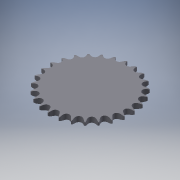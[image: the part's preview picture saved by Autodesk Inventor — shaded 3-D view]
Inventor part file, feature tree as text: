
AUTODESK INVENTOR PART (.ipt)
format: ipt  version: 2016 (Build 200138000, 138)  size: 720,384 bytes
history: native  units: mm
features: other x6, extrude x2, pattern_linear x1, pattern_circular x1
ambient origin geometry x8: Origin, YZ Plane, XZ Plane, XY Plane, X Axis, Y Axis, Z Axis, Center Point
bodies: Solid1 (feature_tree)
feature tree (10):
  other  "Theoretical Tooth Profile"
  other  "Tooth Profile"
  other  "Section Profile"
  other  "Shroud"
  other  "Strand"
  pattern_linear  "Strand Pattern"  Spacing1=109.395135mm  [1 undecoded]
  extrude  "Theoretical Tooth"  Depth=2.327106mm
  extrude  "Tooth"  Depth=4.29755mm
  pattern_circular  "Tooth Pattern"  [2 undecoded]
  other  "Timing Plane"
note: 3 required parameter values undecoded (feature->parameter linkage not recoverable at this tier; creation-order binding heuristic only, values carry confidence <= 0.55)
